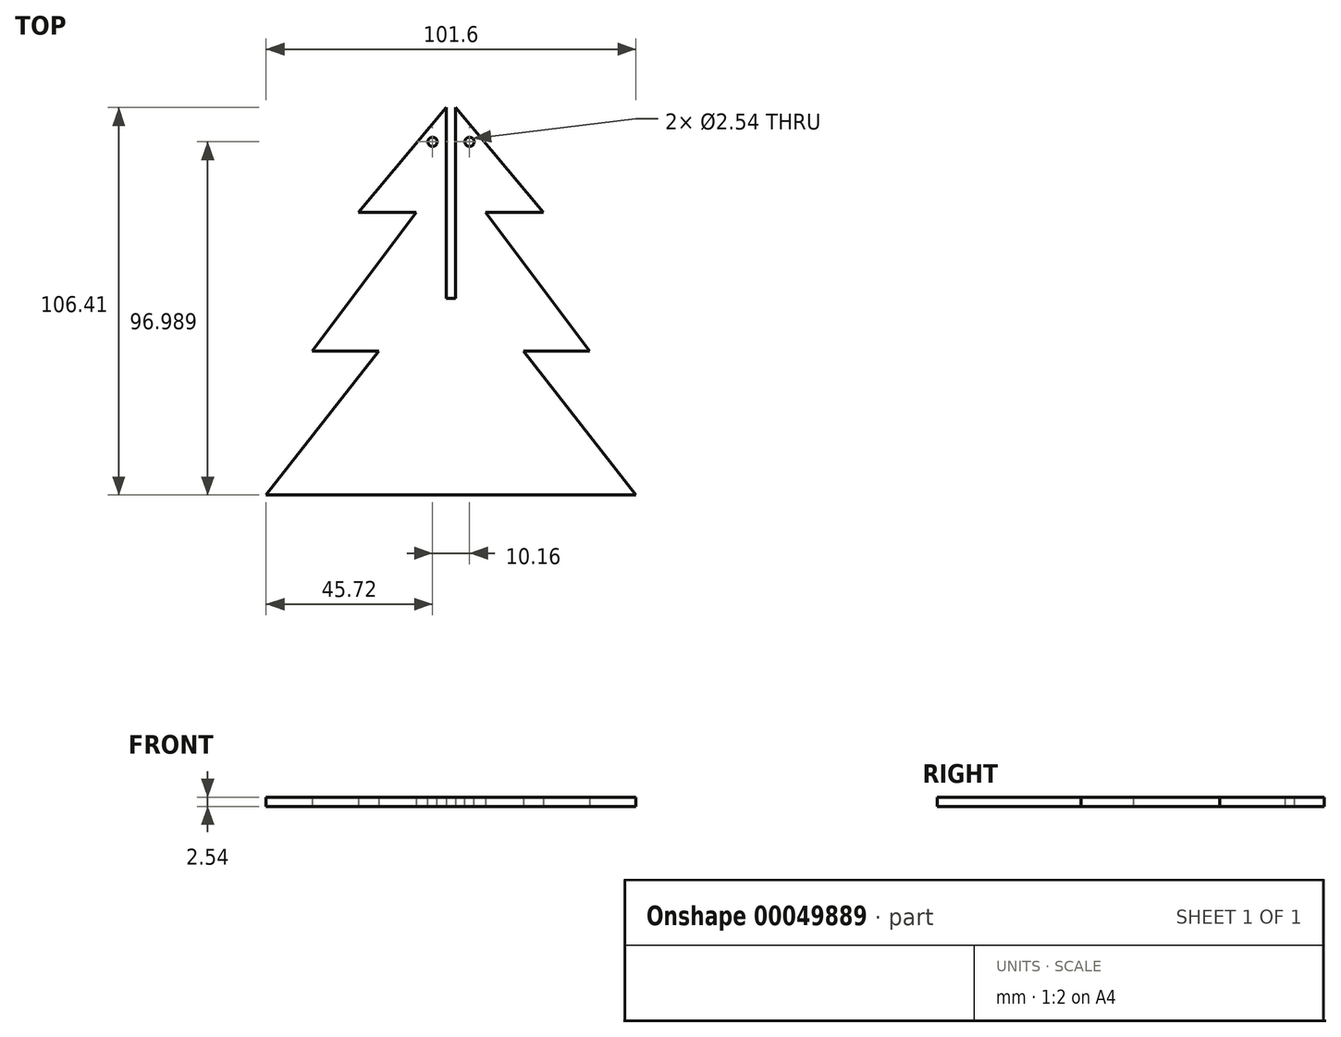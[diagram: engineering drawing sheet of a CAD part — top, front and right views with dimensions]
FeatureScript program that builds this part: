
annotation { "Feature Type Name" : "Feature", "Feature Type Description" : "" }
export const myFeature = defineFeature(function(context is Context, id is Id, definition is map)
    precondition{}
    {
        {
            var Q0;
            Q0=qCreatedBy(makeId("Top.planeOp"),FACE);
            var sketch = newSketch(context, id + "F0", { "sketchPlane" : qUnion([Q0])});
            skLineSegment(sketch, "E0", {"start": v(0, 68.37) * mm, "end": v(-25.4, 38.1) * mm});
            skLineSegment(sketch, "E1", {"start": v(-25.4, 38.1) * mm, "end": v(25.4, 38.1) * mm});
            skLineSegment(sketch, "E2", {"start": v(25.4, 38.1) * mm, "end": v(0, 68.37) * mm});
            skLineSegment(sketch, "E3", {"start": v(0, 50.8) * mm, "end": v(-38.1, 0) * mm});
            skLineSegment(sketch, "E4", {"start": v(-38.1, 0) * mm, "end": v(38.1, 0) * mm});
            skLineSegment(sketch, "E5", {"start": v(38.1, 0) * mm, "end": v(0, 50.8) * mm});
            skLineSegment(sketch, "E6", {"start": v(0, 25.4) * mm, "end": v(-50.8, -39.55) * mm});
            skLineSegment(sketch, "E7", {"start": v(-50.8, -39.55) * mm, "end": v(50.8, -39.55) * mm});
            skLineSegment(sketch, "E8", {"start": v(50.8, -39.55) * mm, "end": v(0, 25.4) * mm});
            skLineSegment(sketch, "E9.bottom", {"start": v(-1.27, 68.37) * mm, "end": v(1.27, 68.37) * mm});
            skLineSegment(sketch, "E9.top", {"start": v(-1.27, 14.4) * mm, "end": v(1.27, 14.4) * mm});
            skLineSegment(sketch, "E9.left", {"start": v(-1.27, 68.37) * mm, "end": v(-1.27, 14.4) * mm});
            skLineSegment(sketch, "E9.right", {"start": v(1.27, 68.37) * mm, "end": v(1.27, 14.4) * mm});
            skSolve(sketch);
        }
        {
            var Q0;
            {var subQ3=sQuery(id+"F0.wireOp",EDGE,"E0");var subQ5=sQuery(id+"F0.wireOp",EDGE,"E1");var subQ7=makeQuery(id+"F0.imprint","INTERSECT",VERTEX,{"derivedFrom":[subQ3,subQ5]});Q0=makeQuery(id+"F0.imprint","IMPRINT",FACE,{"disambiguationData":[TD([[makeQuery(id+"F0.imprint","IMPRINT",EDGE,{"disambiguationData":[TD([[subQ7,1.0]])],"derivedFrom":subQ3}),1.0]])]});}
            var Q1;
            {var subQ3=sQuery(id+"F0.wireOp",EDGE,"E1");var subQ5=sQuery(id+"F0.wireOp",EDGE,"E2");var subQ7=makeQuery(id+"F0.imprint","INTERSECT",VERTEX,{"derivedFrom":[subQ3,subQ5]});Q1=makeQuery(id+"F0.imprint","IMPRINT",FACE,{"disambiguationData":[TD([[makeQuery(id+"F0.imprint","IMPRINT",EDGE,{"disambiguationData":[TD([[subQ7,1.0]])],"derivedFrom":subQ3}),1.0]])]});}
            var Q2;
            {var subQ0=sQuery(id+"F0.wireOp",EDGE,"E5");var subQ3=sQuery(id+"F0.wireOp",EDGE,"E1");var subQ4=makeQuery(id+"F0.imprint","INTERSECT",VERTEX,{"derivedFrom":[subQ3,subQ0]});Q2=makeQuery(id+"F0.imprint","IMPRINT",FACE,{"disambiguationData":[TD([[makeQuery(id+"F0.imprint","IMPRINT",EDGE,{"disambiguationData":[TD([[subQ4,1.0]])],"derivedFrom":subQ3}),1.0]])]});}
            var Q3;
            {var subQ1=sQuery(id+"F0.wireOp",EDGE,"E3");var subQ3=sQuery(id+"F0.wireOp",EDGE,"E1");var subQ5=makeQuery(id+"F0.imprint","INTERSECT",VERTEX,{"derivedFrom":[subQ3,subQ1]});Q3=makeQuery(id+"F0.imprint","IMPRINT",FACE,{"disambiguationData":[TD([[makeQuery(id+"F0.imprint","IMPRINT",EDGE,{"disambiguationData":[TD([[subQ5,-1.0]])],"derivedFrom":subQ3}),1.0]])]});}
            var Q4;
            {var subQ3=sQuery(id+"F0.wireOp",EDGE,"E1");var subQ5=sQuery(id+"F0.wireOp",EDGE,"E3");var subQ6=makeQuery(id+"F0.imprint","INTERSECT",VERTEX,{"derivedFrom":[subQ3,subQ5]});Q4=makeQuery(id+"F0.imprint","IMPRINT",FACE,{"disambiguationData":[TD([[makeQuery(id+"F0.imprint","IMPRINT",EDGE,{"disambiguationData":[TD([[subQ6,-1.0]])],"derivedFrom":subQ3}),-1.0]])]});}
            var Q5;
            {var subQ3=sQuery(id+"F0.wireOp",EDGE,"E1");var subQ5=sQuery(id+"F0.wireOp",EDGE,"E5");var subQ6=makeQuery(id+"F0.imprint","INTERSECT",VERTEX,{"derivedFrom":[subQ3,subQ5]});Q5=makeQuery(id+"F0.imprint","IMPRINT",FACE,{"disambiguationData":[TD([[makeQuery(id+"F0.imprint","IMPRINT",EDGE,{"disambiguationData":[TD([[subQ6,1.0]])],"derivedFrom":subQ3}),-1.0]])]});}
            var Q6;
            {var subQ3=sQuery(id+"F0.wireOp",EDGE,"E9.top");Q6=makeQuery(id+"F0.imprint","IMPRINT",FACE,{"disambiguationData":[TD([[makeQuery(id+"F0.imprint","IMPRINT",EDGE,{"derivedFrom":subQ3}),-1.0]])]});}
            var Q7;
            {var subQ3=sQuery(id+"F0.wireOp",EDGE,"E7");Q7=makeQuery(id+"F0.imprint","IMPRINT",FACE,{"disambiguationData":[TD([[makeQuery(id+"F0.imprint","IMPRINT",EDGE,{"derivedFrom":subQ3}),1.0]])]});}
            extrude(context, id + "F1", {"entities" : qUnion([Q0, Q1, Q2, Q3, Q4, Q5, Q6, Q7]), "depth" : 2.54 * mm});
        }
        {
            var Q0;
            Q0=makeQuery(id+"F1.opExtrude","CAP_FACE",FACE,{"disambiguationData":[OSD([sQuery(id+"F0.wireOp",EDGE,"E0"),sQuery(id+"F0.wireOp",EDGE,"E1"),sQuery(id+"F0.wireOp",EDGE,"E2"),sQuery(id+"F0.wireOp",EDGE,"E3"),sQuery(id+"F0.wireOp",EDGE,"E4"),sQuery(id+"F0.wireOp",EDGE,"E5"),sQuery(id+"F0.wireOp",EDGE,"E6"),sQuery(id+"F0.wireOp",EDGE,"E7"),sQuery(id+"F0.wireOp",EDGE,"E8"),sQuery(id+"F0.wireOp",EDGE,"E9.top"),sQuery(id+"F0.wireOp",EDGE,"E9.left"),sQuery(id+"F0.wireOp",EDGE,"E9.right")])],"isStart":false});
            var sketch = newSketch(context, id + "F2", { "sketchPlane" : qUnion([Q0])});
            skCircle(sketch, "E10", {"center": v(-5.08, 57.44) * mm, "radius": 1.27 * mm});
            skCircle(sketch, "E11.MirrorC", {"center": v(5.08, 57.44) * mm, "radius": 1.27 * mm});
            skSolve(sketch);
        }
        {
            var Q0;
            Q0=sQuery(id+"F2.wireOp",VERTEX,"E10.center");
            var Q1;
            Q1=sQuery(id+"F2.wireOp",VERTEX,"E11.MirrorC.center");
            var Q2;
            Q2=makeQuery(id+"F1.opExtrude","SWEPT_BODY",BODY,{"disambiguationData":[OSD([sQuery(id+"F0.wireOp",EDGE,"E0"),sQuery(id+"F0.wireOp",EDGE,"E1"),sQuery(id+"F0.wireOp",EDGE,"E2"),sQuery(id+"F0.wireOp",EDGE,"E3"),sQuery(id+"F0.wireOp",EDGE,"E4"),sQuery(id+"F0.wireOp",EDGE,"E5"),sQuery(id+"F0.wireOp",EDGE,"E6"),sQuery(id+"F0.wireOp",EDGE,"E7"),sQuery(id+"F0.wireOp",EDGE,"E8"),sQuery(id+"F0.wireOp",EDGE,"E9.top"),sQuery(id+"F0.wireOp",EDGE,"E9.left"),sQuery(id+"F0.wireOp",EDGE,"E9.right")])]});
            hole(context, id + "F3", {"style" : HoleStyle.SIMPLE, "holeDiameter" : 2.54 * mm, "endStyle" : HoleEndStyle.THROUGH, "locations" : qUnion([Q0, Q1]), "scope" : qUnion([Q2])});
        }
    });
